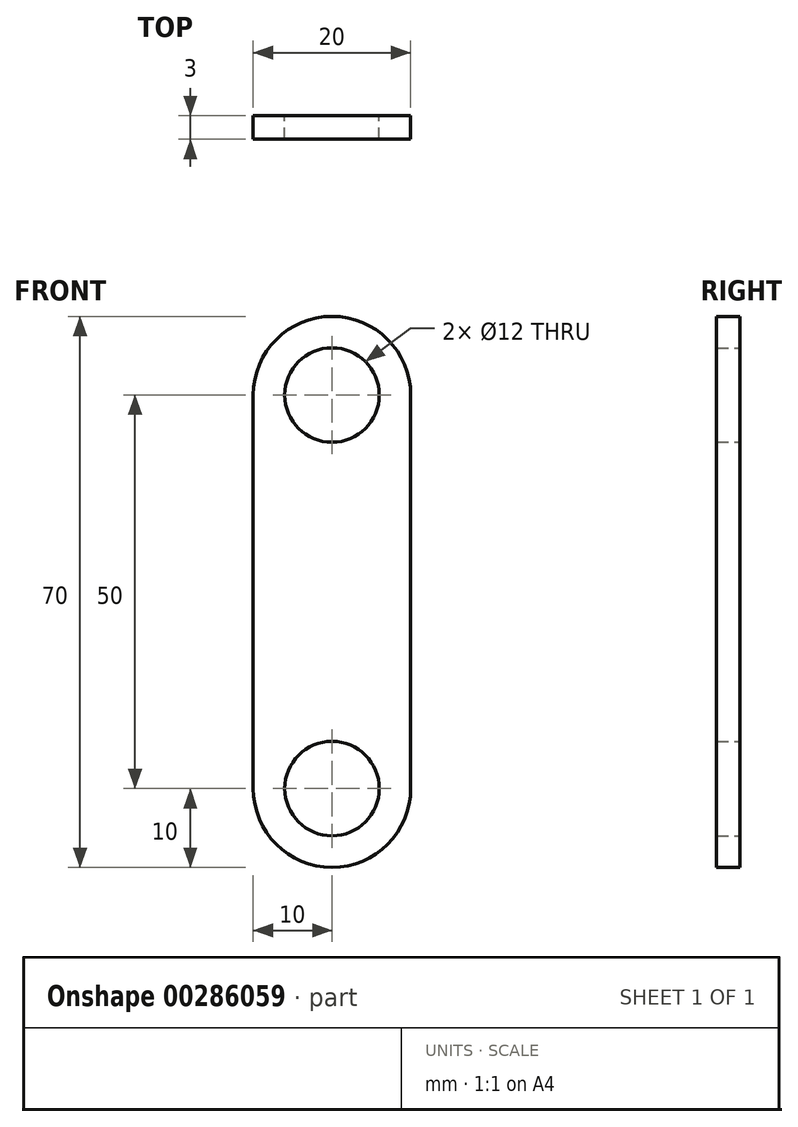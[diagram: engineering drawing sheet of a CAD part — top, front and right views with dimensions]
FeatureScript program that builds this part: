
annotation { "Feature Type Name" : "Feature", "Feature Type Description" : "" }
export const myFeature = defineFeature(function(context is Context, id is Id, definition is map)
    precondition{}
    {
        {
            var Q0;
            Q0=qCreatedBy(makeId("Front.planeOp"),FACE);
            var sketch = newSketch(context, id + "F0", { "sketchPlane" : qUnion([Q0])});
            skLineSegment(sketch, "E0.bottom", {"start": v(10, -25) * mm, "end": v(-10, -25) * mm, "construction": true});
            skLineSegment(sketch, "E0.top", {"start": v(10, 25) * mm, "end": v(-10, 25) * mm, "construction": true});
            skLineSegment(sketch, "E0.left", {"start": v(10, -25) * mm, "end": v(10, 25) * mm});
            skLineSegment(sketch, "E0.right", {"start": v(-10, -25) * mm, "end": v(-10, 25) * mm});
            skPoint(sketch, "E0.middle", {"position": v(0, 0) * mm});
            skArc(sketch, "E1", {"start": v(10, 25) * mm, "mid": v(0, 35) * mm, "end": v(-10, 25) * mm});
            skArc(sketch, "E2", {"start": v(-10, -25) * mm, "mid": v(0, -35) * mm, "end": v(10, -25) * mm});
            skCircle(sketch, "E3", {"center": v(0, -25) * mm, "radius": 6 * mm});
            skCircle(sketch, "E4", {"center": v(0, 25) * mm, "radius": 6 * mm});
            skSolve(sketch);
        }
        {
            var Q0;
            Q0=makeQuery(id+"F0.imprint","IMPRINT",FACE,{"disambiguationData":[TD([[makeQuery(id+"F0.imprint","IMPRINT",EDGE,{"derivedFrom":sQuery(id+"F0.wireOp",EDGE,"E0.left")}),1.0]])]});
            extrude(context, id + "F1", {"entities" : qUnion([Q0]), "depth" : 3 * mm});
        }
    });
